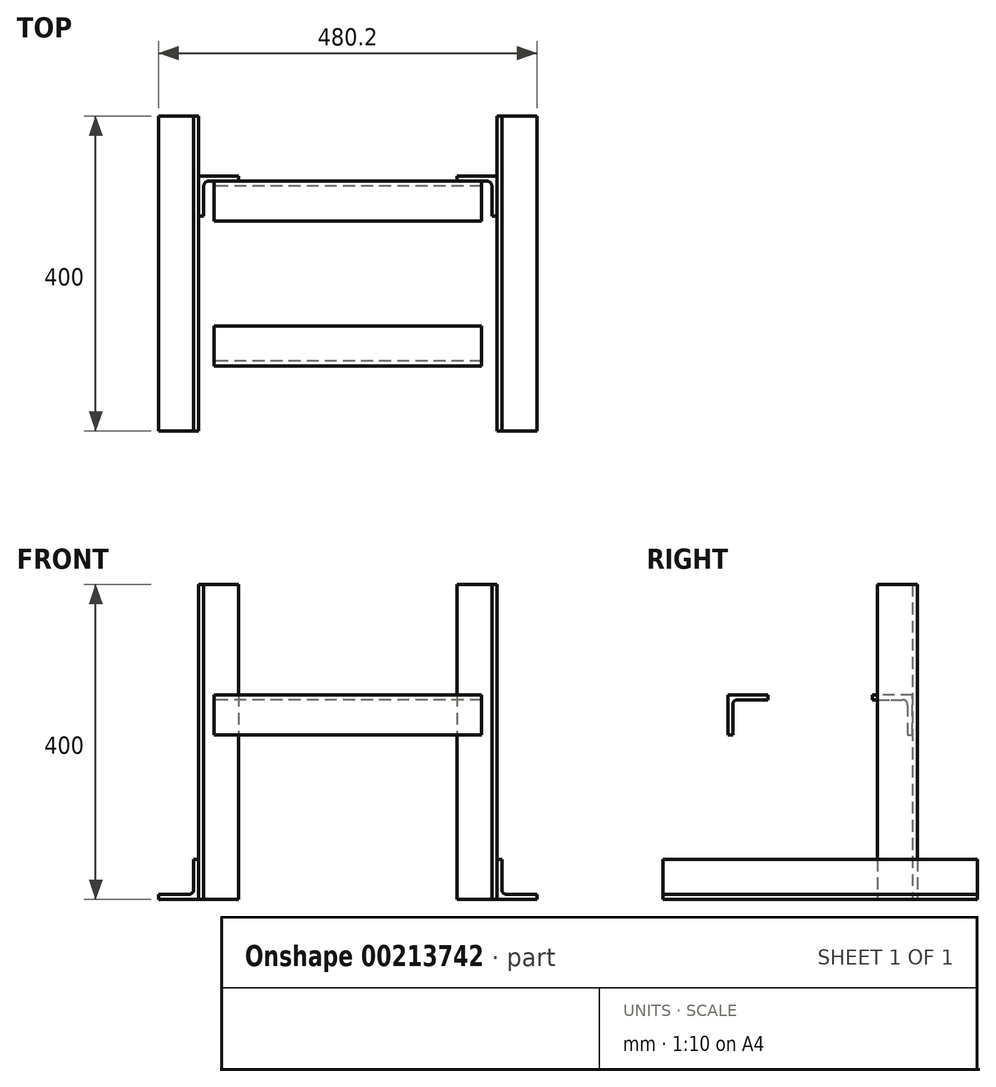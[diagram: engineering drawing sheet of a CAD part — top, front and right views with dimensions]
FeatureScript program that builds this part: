
annotation { "Feature Type Name" : "Feature", "Feature Type Description" : "" }
export const myFeature = defineFeature(function(context is Context, id is Id, definition is map)
    precondition{}
    {
        {
            var Q0;
            Q0=qCreatedBy(makeId("Front.planeOp"),FACE);
            var sketch = newSketch(context, id + "F0", { "sketchPlane" : qUnion([Q0])});
            skLineSegment(sketch, "E0", {"start": v(0, 0) * mm, "end": v(-189.3, 0) * mm, "construction": true});
            skLineSegment(sketch, "E1", {"start": v(-189.3, 0) * mm, "end": v(-189.3, 50.8) * mm});
            skLineSegment(sketch, "E2", {"start": v(-189.3, 50.8) * mm, "end": v(-195.65, 50.8) * mm});
            skLineSegment(sketch, "E3", {"start": v(-195.65, 50.8) * mm, "end": v(-195.65, 12.7) * mm});
            skLineSegment(sketch, "E4", {"start": v(-202, 6.35) * mm, "end": v(-240.1, 6.35) * mm});
            skLineSegment(sketch, "E5", {"start": v(-240.1, 6.35) * mm, "end": v(-240.1, 0) * mm});
            skLineSegment(sketch, "E6", {"start": v(-240.1, 0) * mm, "end": v(-189.3, 0) * mm});
            skPoint(sketch, "E7.visualSharp", {"position": v(-195.65, 6.35) * mm});
            skArc(sketch, "E7.filletArc", {"start": v(-202, 6.35) * mm, "mid": v(-197.5, 8.2) * mm, "end": v(-195.65, 12.7) * mm});
            skSolve(sketch);
        }
        {
            var Q0;
            Q0=makeQuery(id+"F0.imprint","IMPRINT",FACE,{"disambiguationData":[TD([[makeQuery(id+"F0.imprint","IMPRINT",EDGE,{"derivedFrom":sQuery(id+"F0.wireOp",EDGE,"E1")}),1.0]])]});
            extrude(context, id + "F1", {"entities" : qUnion([Q0]), "endBound" : BoundingType.SYMMETRIC, "depth" : 400 * mm});
        }
        {
            var Q0;
            Q0=qCreatedBy(makeId("Top.planeOp"),FACE);
            var sketch = newSketch(context, id + "F2", { "sketchPlane" : qUnion([Q0])});
            skLineSegment(sketch, "E8", {"start": v(-189.3, 123.8) * mm, "end": v(-138.5, 123.8) * mm});
            skLineSegment(sketch, "E9", {"start": v(-138.5, 123.8) * mm, "end": v(-138.5, 117.45) * mm});
            skLineSegment(sketch, "E10", {"start": v(-138.5, 117.45) * mm, "end": v(-176.6, 117.45) * mm});
            skLineSegment(sketch, "E11", {"start": v(-182.95, 111.1) * mm, "end": v(-182.95, 73) * mm});
            skLineSegment(sketch, "E12", {"start": v(-182.95, 73) * mm, "end": v(-189.3, 73) * mm});
            skLineSegment(sketch, "E13", {"start": v(-189.3, 73) * mm, "end": v(-189.3, 123.8) * mm});
            skPoint(sketch, "E14.visualSharp", {"position": v(-182.95, 117.45) * mm});
            skArc(sketch, "E14.filletArc", {"start": v(-176.6, 117.45) * mm, "mid": v(-181.1, 115.6) * mm, "end": v(-182.95, 111.1) * mm});
            skSolve(sketch);
        }
        {
            var Q0;
            Q0 = qSketchRegion(id + "F2", true);
            extrude(context, id + "F3", {"entities" : qUnion([Q0]), "operationType" : NewBodyOperationType.ADD, "depth" : 400 * mm});
        }
        {
            var Q0;
            Q0=makeQuery(id+"F1.opExtrude","SWEPT_BODY",BODY,{"disambiguationData":[OSD([sQuery(id+"F0.wireOp",EDGE,"E1"),sQuery(id+"F0.wireOp",EDGE,"E2"),sQuery(id+"F0.wireOp",EDGE,"E3"),sQuery(id+"F0.wireOp",EDGE,"E4"),sQuery(id+"F0.wireOp",EDGE,"E5"),sQuery(id+"F0.wireOp",EDGE,"E6"),sQuery(id+"F0.wireOp",EDGE,"E7.filletArc")])]});
            var Q1;
            Q1=qCreatedBy(makeId("Right.planeOp"),FACE);
            mirror(context, id + "F4", {"entities" : qUnion([Q0]), "mirrorPlane" : qUnion([Q1])});
        }
        {
            var Q0;
            Q0=qCreatedBy(makeId("Right.planeOp"),FACE);
            var sketch = newSketch(context, id + "F5", { "sketchPlane" : qUnion([Q0])});
            skLineSegment(sketch, "E15", {"start": v(-117.45, 260) * mm, "end": v(-66.65, 260) * mm});
            skLineSegment(sketch, "E16", {"start": v(-66.65, 260) * mm, "end": v(-66.65, 253.65) * mm});
            skLineSegment(sketch, "E17", {"start": v(-66.65, 253.65) * mm, "end": v(-104.75, 253.65) * mm});
            skLineSegment(sketch, "E18", {"start": v(-111.1, 247.3) * mm, "end": v(-111.1, 209.2) * mm});
            skLineSegment(sketch, "E19", {"start": v(-111.1, 209.2) * mm, "end": v(-117.45, 209.2) * mm});
            skLineSegment(sketch, "E20", {"start": v(-117.45, 209.2) * mm, "end": v(-117.45, 260) * mm});
            skPoint(sketch, "E21.visualSharp", {"position": v(-111.1, 253.65) * mm});
            skArc(sketch, "E21.filletArc", {"start": v(-104.75, 253.65) * mm, "mid": v(-109.24, 251.8) * mm, "end": v(-111.1, 247.3) * mm});
            skSolve(sketch);
        }
        {
            var Q0;
            Q0=makeQuery(id+"F5.imprint","IMPRINT",FACE,{"disambiguationData":[TD([[makeQuery(id+"F5.imprint","IMPRINT",EDGE,{"derivedFrom":sQuery(id+"F5.wireOp",EDGE,"E15")}),-1.0]])]});
            extrude(context, id + "F6", {"entities" : qUnion([Q0]), "endBound" : BoundingType.SYMMETRIC, "depth" : 340 * mm});
        }
        {
            var Q0;
            Q0=makeQuery(id+"F6.opExtrude","SWEPT_BODY",BODY,{"disambiguationData":[OSD([sQuery(id+"F5.wireOp",EDGE,"E15"),sQuery(id+"F5.wireOp",EDGE,"E16"),sQuery(id+"F5.wireOp",EDGE,"E17"),sQuery(id+"F5.wireOp",EDGE,"E18"),sQuery(id+"F5.wireOp",EDGE,"E19"),sQuery(id+"F5.wireOp",EDGE,"E20"),sQuery(id+"F5.wireOp",EDGE,"E21.filletArc")])]});
            var Q1;
            Q1=qCreatedBy(makeId("Front.planeOp"),FACE);
            mirror(context, id + "F7", {"entities" : qUnion([Q0]), "mirrorPlane" : qUnion([Q1])});
        }
    });
